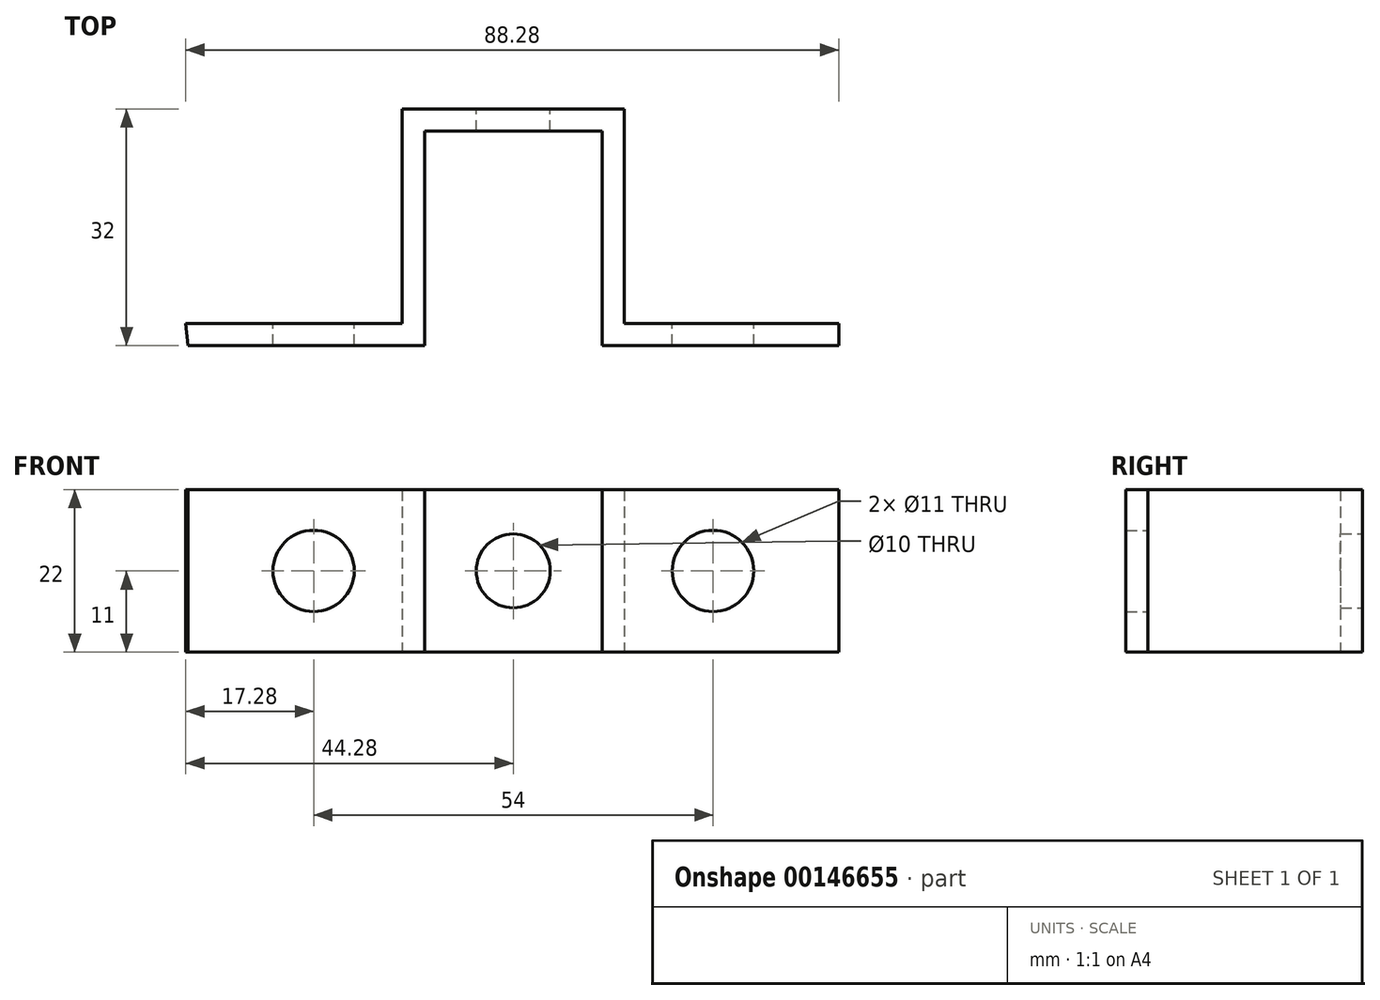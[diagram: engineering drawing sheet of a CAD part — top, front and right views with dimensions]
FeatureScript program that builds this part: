
annotation { "Feature Type Name" : "Feature", "Feature Type Description" : "" }
export const myFeature = defineFeature(function(context is Context, id is Id, definition is map)
    precondition{}
    {
        {
            var Q0;
            Q0=qCreatedBy(makeId("Top.planeOp"),FACE);
            var sketch = newSketch(context, id + "F0", { "sketchPlane" : qUnion([Q0])});
            skLineSegment(sketch, "E0", {"start": v(-44.28, -15.63) * mm, "end": v(-15, -15.63) * mm});
            skLineSegment(sketch, "E1", {"start": v(-15, -15.63) * mm, "end": v(-15, 13.37) * mm});
            skLineSegment(sketch, "E2", {"start": v(-15, 13.37) * mm, "end": v(15, 13.37) * mm});
            skLineSegment(sketch, "E3", {"start": v(15, 13.37) * mm, "end": v(15, -15.63) * mm});
            skLineSegment(sketch, "E4", {"start": v(15, -15.63) * mm, "end": v(44, -15.63) * mm});
            skLineSegment(sketch, "E5", {"start": v(44, -15.63) * mm, "end": v(44, -18.63) * mm});
            skLineSegment(sketch, "E6", {"start": v(44, -18.63) * mm, "end": v(12, -18.63) * mm});
            skLineSegment(sketch, "E7", {"start": v(12, -18.63) * mm, "end": v(12, 10.37) * mm});
            skLineSegment(sketch, "E8", {"start": v(12, 10.37) * mm, "end": v(-12, 10.37) * mm});
            skLineSegment(sketch, "E9", {"start": v(-12, 10.37) * mm, "end": v(-12, -18.63) * mm});
            skLineSegment(sketch, "E10", {"start": v(-12, -18.63) * mm, "end": v(-44, -18.63) * mm});
            skLineSegment(sketch, "E11", {"start": v(-44, -18.63) * mm, "end": v(-44.28, -15.63) * mm});
            skSolve(sketch);
        }
        {
            var Q0;
            Q0=makeQuery(id+"F0.imprint","IMPRINT",FACE,{"disambiguationData":[TD([[makeQuery(id+"F0.imprint","IMPRINT",EDGE,{"derivedFrom":sQuery(id+"F0.wireOp",EDGE,"E0")}),-1.0]])]});
            extrude(context, id + "F1", {"entities" : qUnion([Q0]), "depth" : 22 * mm});
        }
        {
            var Q0;
            Q0=makeQuery(id+"F1.opExtrude","SWEPT_FACE",FACE,{"disambiguationData":[OSD([sQuery(id+"F0.wireOp",EDGE,"E2")])]});
            var sketch = newSketch(context, id + "F2", { "sketchPlane" : qUnion([Q0])});
            skCircle(sketch, "E12", {"center": v(0, 11) * mm, "radius": 5 * mm});
            skSolve(sketch);
        }
        {
            var Q0;
            Q0=makeQuery(id+"F2.imprint","IMPRINT",FACE,{"disambiguationData":[TD([[makeQuery(id+"F2.imprint","IMPRINT",EDGE,{"derivedFrom":sQuery(id+"F2.wireOp",EDGE,"E12")}),1.0]])]});
            var Q1;
            Q1=makeQuery(id+"F2.imprint","IMPRINT",FACE,{"disambiguationData":[TD([[makeQuery(id+"F2.imprint","IMPRINT",EDGE,{"derivedFrom":sQuery(id+"F2.wireOp",EDGE,"SnFEwmQJ-0jKd-7hRC-Gs63-dFjEfwIYBr6G")}),1.0]])]});
            var Q2;
            Q2=makeQuery(id+"F2.imprint","IMPRINT",FACE,{"disambiguationData":[TD([[makeQuery(id+"F2.imprint","IMPRINT",EDGE,{"derivedFrom":sQuery(id+"F2.wireOp",EDGE,"s0sbz3Wh-nNE4-peUs-16b5-eVxWWiYI7D4N")}),1.0]])]});
            extrude(context, id + "F3", {"entities" : qUnion([Q0, Q1, Q2]), "operationType" : NewBodyOperationType.REMOVE, "oppositeDirection" : true, "depth" : 10 * mm});
        }
        {
            var Q0;
            Q0=qCreatedBy(makeId("Front.planeOp"),FACE);
            var sketch = newSketch(context, id + "F4", { "sketchPlane" : qUnion([Q0])});
            skCircle(sketch, "E13", {"center": v(27, 11) * mm, "radius": 5.5 * mm});
            skCircle(sketch, "E14", {"center": v(-27, 11) * mm, "radius": 5.5 * mm});
            skArc(sketch, "E15", {"start": v(-26.81, 21.75) * mm, "mid": v(-38.55, 13.42) * mm, "end": v(-43.72, 0) * mm});
            skSolve(sketch);
        }
        {
            var Q0;
            Q0 = qSketchRegion(id + "F4", true);
            extrude(context, id + "F5", {"entities" : qUnion([Q0]), "operationType" : NewBodyOperationType.REMOVE, "depth" : 25 * mm});
        }
    });
